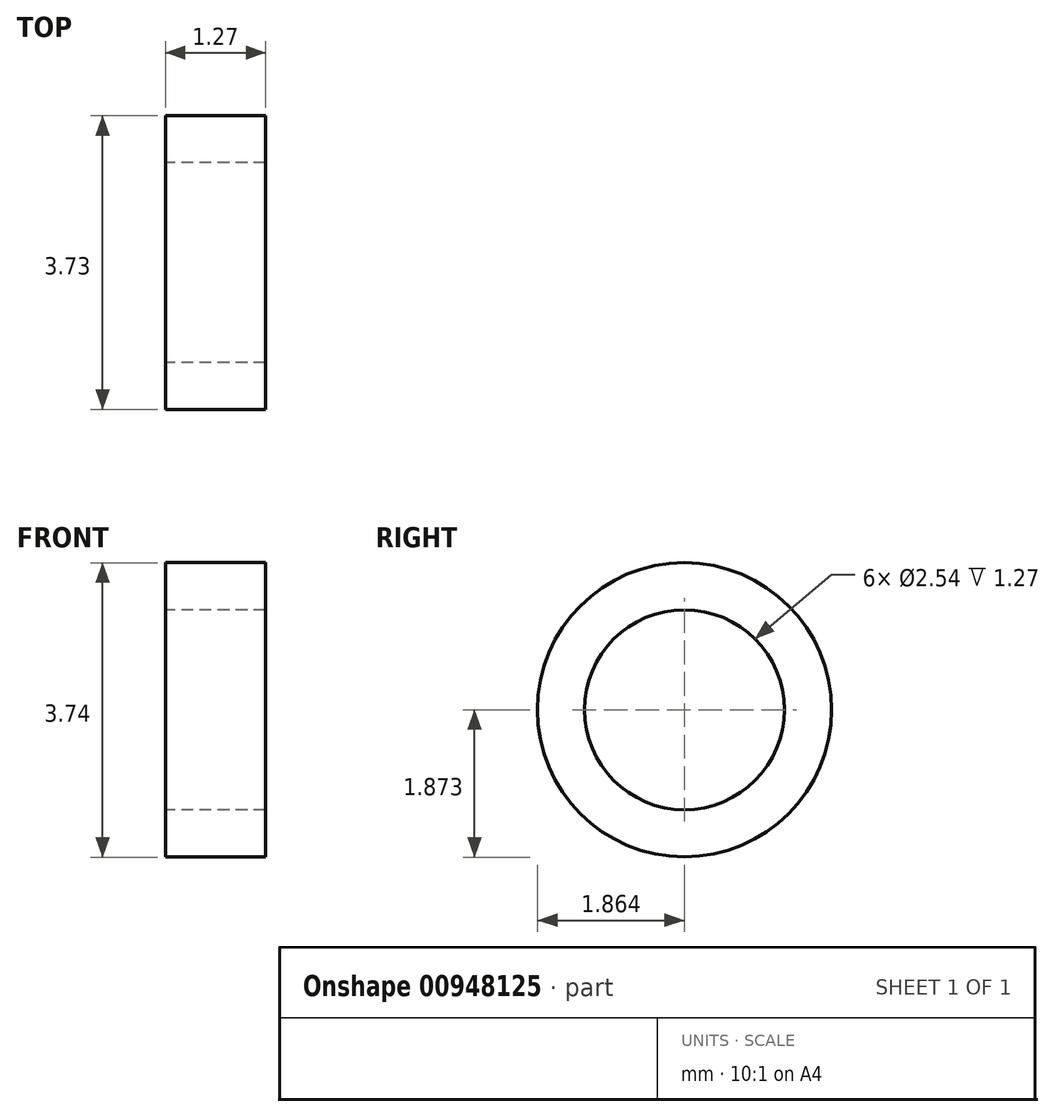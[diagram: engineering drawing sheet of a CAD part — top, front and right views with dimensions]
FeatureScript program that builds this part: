
annotation { "Feature Type Name" : "Feature", "Feature Type Description" : "" }
export const myFeature = defineFeature(function(context is Context, id is Id, definition is map)
    precondition{}
    {
        {
            var Q0;
            Q0=qCreatedBy(makeId("Right.planeOp"),FACE);
            var sketch = newSketch(context, id + "F0", { "sketchPlane" : qUnion([Q0])});
            skCircle(sketch, "E0", {"center": v(-21.55, 16) * mm, "radius": 1.87 * mm});
            skCircle(sketch, "E1", {"center": v(-21.55, 16) * mm, "radius": 1.27 * mm});
            skSolve(sketch);
        }
        {
            var Q0;
            Q0=makeQuery(id+"F0.imprint","IMPRINT",FACE,{"disambiguationData":[TD([[makeQuery(id+"F0.imprint","IMPRINT",EDGE,{"derivedFrom":sQuery(id+"F0.wireOp",EDGE,"E0")}),1.0]])]});
            extrude(context, id + "F1", {"entities" : qUnion([Q0]), "depth" : 1.27 * mm, "offsetDistance" : 25.4 * mm});
        }
    });
